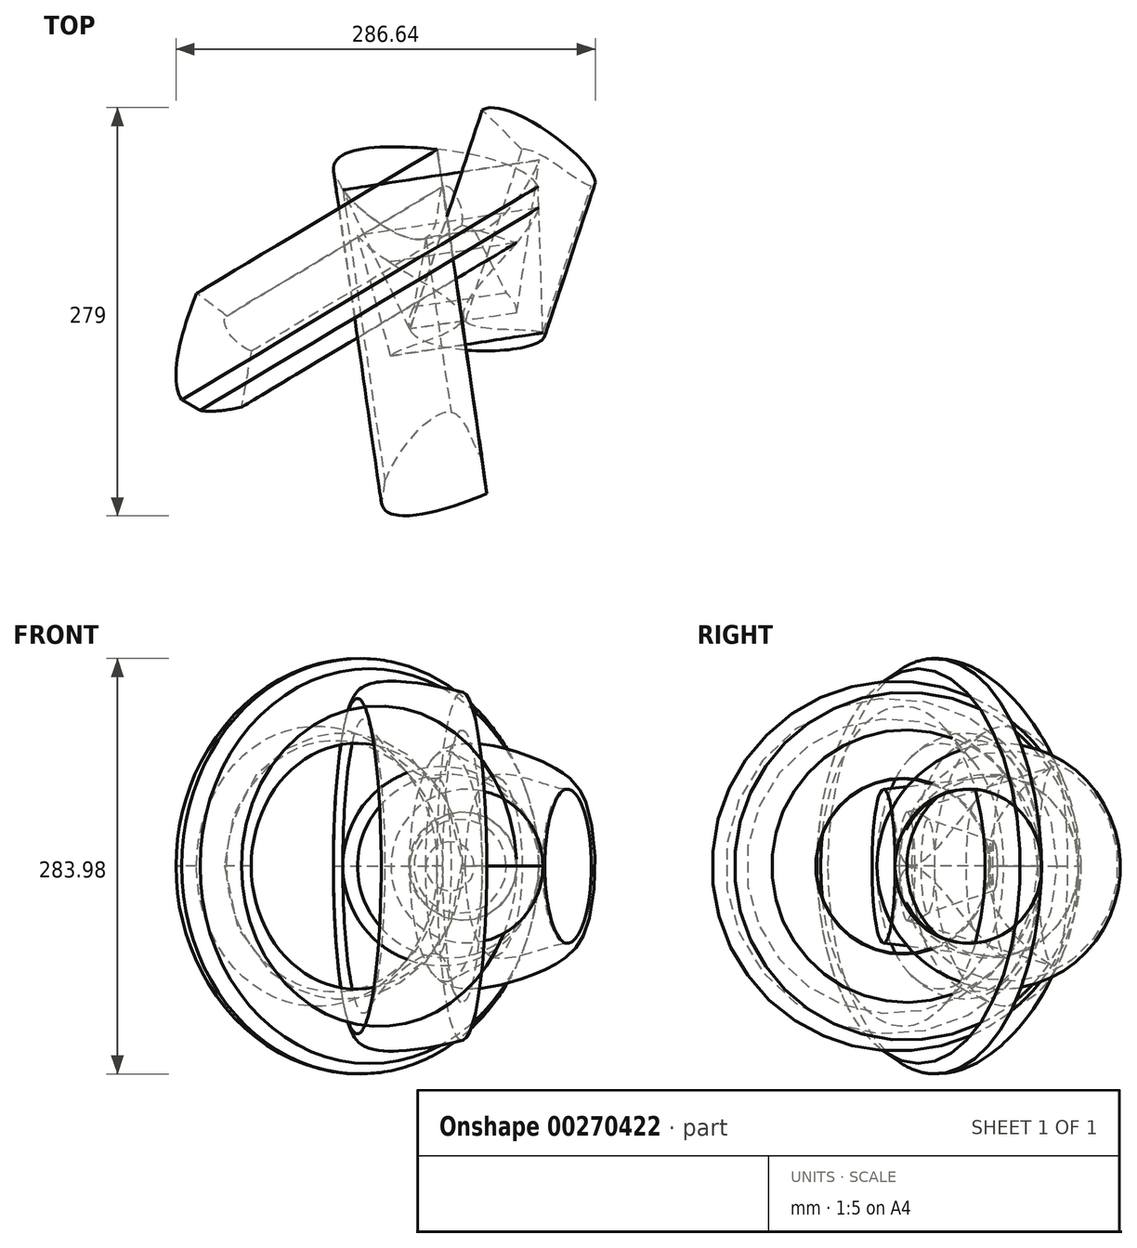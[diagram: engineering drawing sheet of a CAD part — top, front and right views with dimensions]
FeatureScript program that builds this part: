
annotation { "Feature Type Name" : "Feature", "Feature Type Description" : "" }
export const myFeature = defineFeature(function(context is Context, id is Id, definition is map)
    precondition{}
    {
        {
            var Q0;
            Q0=qCreatedBy(makeId("Top.planeOp"),FACE);
            var sketch = newSketch(context, id + "F0", { "sketchPlane" : qUnion([Q0])});
            skFitSpline(sketch, "E0", {"points": [v(0, 0) * mm, v(-63.18, 45.93) * mm, v(7.74, 60.44) * mm, v(76.72, 34.97) * mm, v(61.89, -3.38) * mm, v(27.08, -56.9) * mm, v(79.94, -64.95) * mm, v(72.53, -73.33) * mm, v(-10.96, -62.37) * mm, v(24.82, 8.86) * mm, v(11.6, 34.97) * mm, v(0, 0) * mm]});
            skLineSegment(sketch, "E1", {"start": v(11.6, 34.97) * mm, "end": v(7.74, 60.44) * mm});
            skLineSegment(sketch, "E2", {"start": v(24.82, 8.86) * mm, "end": v(61.89, -3.38) * mm});
            skLineSegment(sketch, "E3", {"start": v(79.94, -64.95) * mm, "end": v(76.72, 34.97) * mm});
            skLineSegment(sketch, "E4", {"start": v(0, 0) * mm, "end": v(-10.96, -62.37) * mm});
            skLineSegment(sketch, "E5", {"start": v(27.08, -56.9) * mm, "end": v(-10.96, -62.37) * mm});
            skLineSegment(sketch, "E6", {"start": v(-10.96, -62.37) * mm, "end": v(-63.18, 45.93) * mm});
            skLineSegment(sketch, "E7", {"start": v(-63.82, -6.6) * mm, "end": v(-45.13, -37.87) * mm});
            skSolve(sketch);
        }
        {
            var Q0;
            {var subQ0=sQuery(id+"F0.wireOp",EDGE,"E1");Q0=makeQuery(id+"F0.imprint","IMPRINT",FACE,{"disambiguationData":[TD([[makeQuery(id+"F0.imprint","IMPRINT",EDGE,{"derivedFrom":subQ0}),1.0]])]});}
            var Q1;
            Q1=sQuery(id+"F0.wireOp",EDGE,"E5");
            revolve(context, id + "F1", {"entities" : qUnion([Q0]), "axis" : qUnion([Q1]), "revolveType" : RevolveType.FULL});
        }
        {
            var Q0;
            {var subQ0=sQuery(id+"F0.wireOp",EDGE,"E1");Q0=makeQuery(id+"F0.imprint","IMPRINT",FACE,{"disambiguationData":[TD([[makeQuery(id+"F0.imprint","IMPRINT",EDGE,{"derivedFrom":subQ0}),-1.0]])]});}
            var Q1;
            Q1=sQuery(id+"F0.wireOp",EDGE,"E7");
            revolve(context, id + "F2", {"entities" : qUnion([Q0]), "axis" : qUnion([Q1]), "revolveType" : RevolveType.FULL});
        }
        {
            var Q0;
            {var subQ2=sQuery(id+"F0.wireOp",EDGE,"E5");Q0=makeQuery(id+"F0.imprint","IMPRINT",FACE,{"disambiguationData":[TD([[makeQuery(id+"F0.imprint","IMPRINT",EDGE,{"derivedFrom":subQ2}),1.0]])]});}
            var Q1;
            Q1=sQuery(id+"F0.wireOp",EDGE,"E2");
            revolve(context, id + "F3", {"entities" : qUnion([Q0]), "axis" : qUnion([Q1]), "revolveType" : RevolveType.FULL});
        }
        {
            var Q0;
            {var subQ0=sQuery(id+"F0.wireOp",EDGE,"E4");var subQ1=sQuery(id+"F0.wireOp",EDGE,"E0");var subQ2=makeQuery(id+"F0.imprint","INTERSECT",VERTEX,{"disambiguationData":[OD(0.0)],"derivedFrom":[subQ1,subQ0]});Q0=makeQuery(id+"F0.imprint","IMPRINT",FACE,{"disambiguationData":[TD([[makeQuery(id+"F0.imprint","IMPRINT",EDGE,{"disambiguationData":[TD([[subQ2,-1.0]])],"derivedFrom":subQ1}),1.0]])]});}
            var Q1;
            Q1=sQuery(id+"F0.wireOp",EDGE,"E1");
            revolve(context, id + "F4", {"entities" : qUnion([Q0]), "axis" : qUnion([Q1]), "revolveType" : RevolveType.FULL});
        }
        {
            var Q0;
            {var subQ0=sQuery(id+"F0.wireOp",EDGE,"E0");var subQ1=makeQuery(id+"F0.imprint","INTERSECT",VERTEX,{"disambiguationData":[OD(1.0)],"derivedFrom":[subQ0,sQuery(id+"F0.wireOp",EDGE,"E2")]});Q0=makeQuery(id+"F0.imprint","IMPRINT",FACE,{"disambiguationData":[TD([[makeQuery(id+"F0.imprint","IMPRINT",EDGE,{"disambiguationData":[TD([[subQ1,1.0]])],"derivedFrom":subQ0}),1.0]])]});}
            var Q1;
            Q1=sQuery(id+"F0.wireOp",EDGE,"E1");
            revolve(context, id + "F5", {"entities" : qUnion([Q0]), "axis" : qUnion([Q1]), "revolveType" : RevolveType.FULL});
        }
    });
